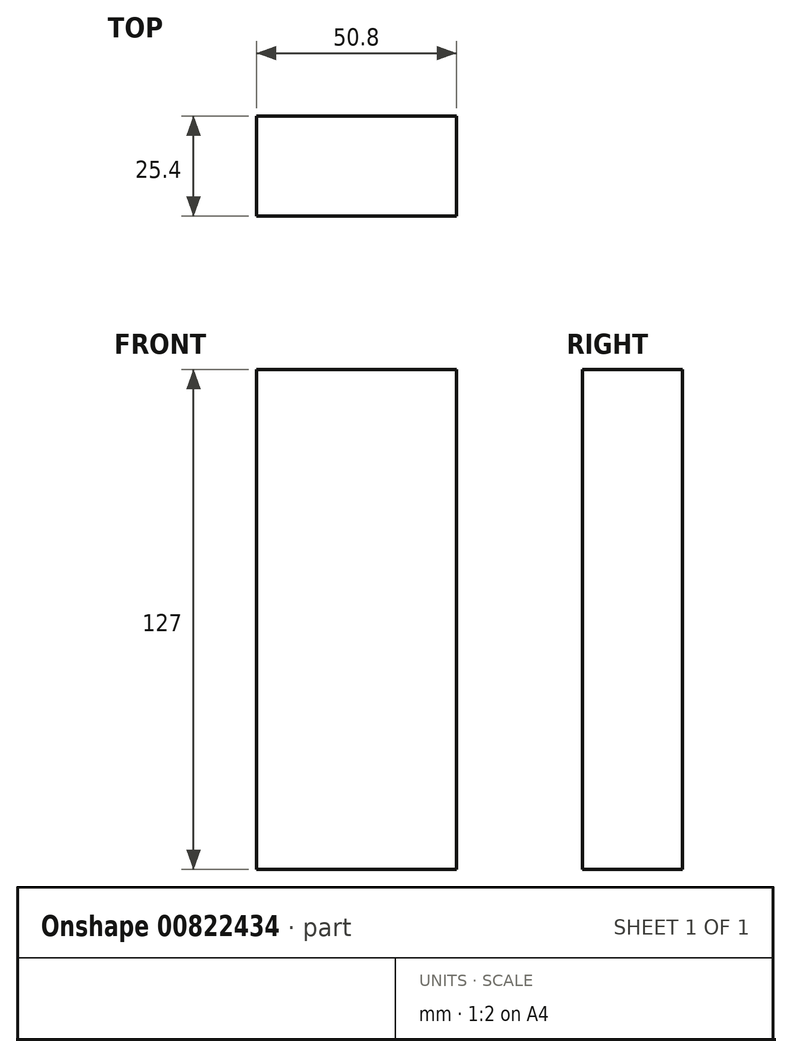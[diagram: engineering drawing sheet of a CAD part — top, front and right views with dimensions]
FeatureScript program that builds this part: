
annotation { "Feature Type Name" : "Feature", "Feature Type Description" : "" }
export const myFeature = defineFeature(function(context is Context, id is Id, definition is map)
    precondition{}
    {
        {
            var Q0;
            Q0=qCreatedBy(makeId("Top.planeOp"),FACE);
            var sketch = newSketch(context, id + "F0", { "sketchPlane" : qUnion([Q0])});
            skLineSegment(sketch, "E0.bottom", {"start": v(0, 0) * mm, "end": v(50.8, 0) * mm});
            skLineSegment(sketch, "E0.top", {"start": v(0, 25.4) * mm, "end": v(50.8, 25.4) * mm});
            skLineSegment(sketch, "E0.left", {"start": v(0, 0) * mm, "end": v(0, 25.4) * mm});
            skLineSegment(sketch, "E0.right", {"start": v(50.8, 0) * mm, "end": v(50.8, 25.4) * mm});
            skSolve(sketch);
        }
        {
            var Q0;
            Q0=makeQuery(id+"F0.imprint","IMPRINT",FACE,{"disambiguationData":[TD([[makeQuery(id+"F0.imprint","IMPRINT",EDGE,{"derivedFrom":sQuery(id+"F0.wireOp",EDGE,"E0.bottom")}),1.0]])]});
            extrude(context, id + "F1", {"entities" : qUnion([Q0]), "depth" : 127 * mm, "offsetDistance" : 25.4 * mm});
        }
    });
